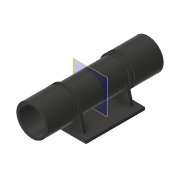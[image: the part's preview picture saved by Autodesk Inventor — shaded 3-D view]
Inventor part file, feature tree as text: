
AUTODESK INVENTOR PART (.ipt)
format: ipt  version: 2019.4 (Build 234330000, 330)  size: 185,856 bytes
history: native  units: mm
features: sketch x4, projected_geometry x4, extrude x3, mirror x2, revolve x1, plane x1
ambient origin geometry x8: Origin, YZ Plane, XZ Plane, XY Plane, X Axis, Y Axis, Z Axis, Center Point
bodies: Solid1 (feature_tree)
feature tree (15):
  revolve  "Revolution1"  [1 undecoded]
  extrude  "Extrusion1"  Depth=9.9mm
  mirror  "Mirror1"
  plane  "Work Plane1"
  extrude  "Extrusion2"  Depth=1.0mm
  mirror  "Mirror2"
  extrude  "Extrusion3"  TaperAngle=90.0deg  [1 undecoded]
  sketch  "Sketch1"  dims[d1=20.0mm d2=11.0mm]
  sketch  "Sketch2"  dims[d3=20.0mm d4=9.9mm]
  projected_geometry  "Projected Loop1"
  sketch  "Sketch3"  dims[d6=2.5mm d7=1.0mm]
  projected_geometry  "Projected Loop2"
  sketch  "Sketch4"  dims[d8=0.0mm d9=90.0deg d10=10.0mm d11=-0.872665mm d12=13.0mm d13=105.0deg d14=75.0deg d15=2.0mm d16=0.0mm d17=2.0mm d18=0.0mm d19=17.75mm d20=1.8mm d21=13.5mm]
  projected_geometry  "Projected Loop3"
  projected_geometry  "Projected Loop4"
note: 2 required parameter values undecoded (feature->parameter linkage not recoverable at this tier; creation-order binding heuristic only, values carry confidence <= 0.55)